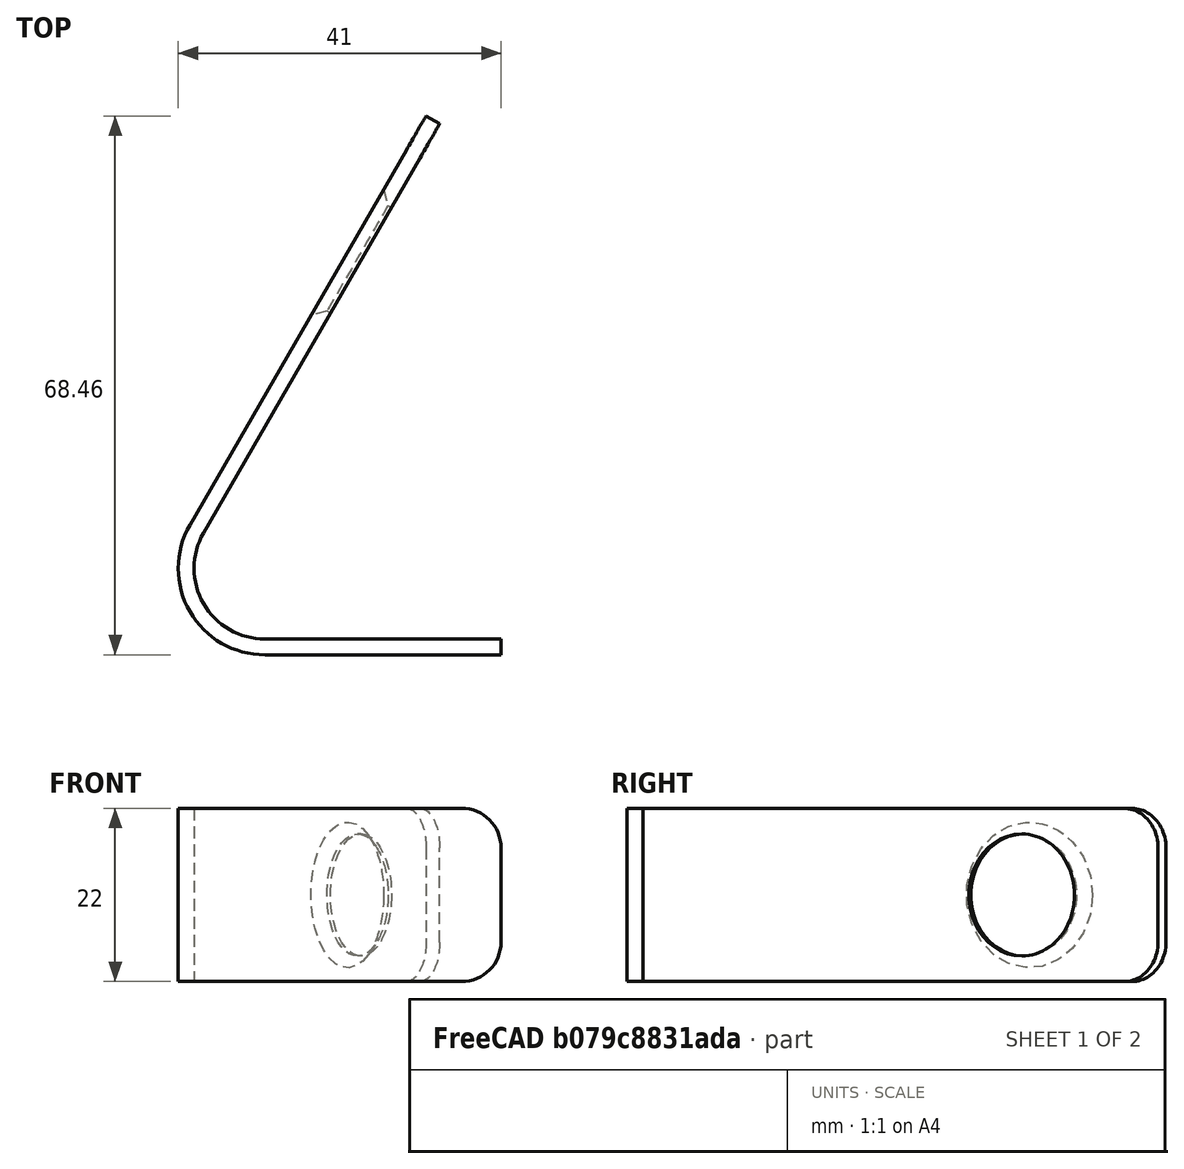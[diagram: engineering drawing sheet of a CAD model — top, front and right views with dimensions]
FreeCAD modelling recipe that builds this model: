
FCSTD DOCUMENT  (FreeCAD 2021.1015R24301 +3962 (Git))
Label: plastic_spring_catapult_2
License: All rights reserved
objects: Sketcher::SketchObject×3, Spreadsheet::Sheet×1, PartDesign::AdditivePipe×1, PartDesign::Pocket×1, PartDesign::Chamfer×1, PartDesign::Fillet×1, PartDesign::Body×1, Mesh::Feature×1
note: 16 computed .brp shape members not serialized (recipe doc carries the construction recipe); baked Part::Feature solids carry a one-line shape summary decoded from their .brp

FEATURE [Spreadsheet::Sheet] Spreadsheet
  PythonMode = false
  cells = A1='width; B1(w)=22; A2='thickness; B2(thk)=2; A3='dia; B3(dia)=10; A4=arm length; B4(l_arm)=60; A5=base length; B5(base_length)=30; A6=catapult angle; B6(a_catapult)=60; A7=bottom curve diameter; B7(dia_bot)=20; A8='marble_diameter; B8(d_marble)=16.4; A9=depth of marble pocket; B9(cup_depth)=8; A10=cup distance from end of arm; B10(l_cup)=20; A11=cup dia; B11(d_cup)=15.5
FEATURE [Sketcher::SketchObject] Sketch  label="profile"
  FullyConstrained = true
  MapMode = 5
  Placement = pos=(0,0,0) rot=(0.57735,0.57735,0.57735;2.0944rad)
  Support = -> [YZ_Plane]
  expr: Constraints[10] = Spreadsheet.thk / 2
  expr: Constraints[11] = Spreadsheet.thk
  expr: Constraints[9] = Spreadsheet.w
  sketch-geometry (4):
    g0: LineSegment StartX=-1 StartY=0 StartZ=0 EndX=1 EndY=0 EndZ=0
    g1: LineSegment StartX=1 StartY=0 StartZ=0 EndX=1 EndY=22 EndZ=0
    g2: LineSegment StartX=1 StartY=22 StartZ=0 EndX=-1 EndY=22 EndZ=0
    g3: LineSegment StartX=-1 StartY=22 StartZ=0 EndX=-1 EndY=0 EndZ=0
  constraints (12):
    c: Coincident(g0,g1)
    c: Coincident(g1,g2)
    c: Coincident(g2,g3)
    c: Coincident(g3,g0)
    c: Horizontal(g0)
    c: Horizontal(g2)
    c: Vertical(g1)
    c: Vertical(g3)
    c: PointOnObject(g0,g-1)
    c: DistanceY(g3,g3) = 22
    c: DistanceX(g0,g-1) = 1
    c: DistanceX(g0,g0) = 2
FEATURE [Sketcher::SketchObject] Sketch001  label="path"
  FullyConstrained = true
  MapMode = 5
  Support = -> [XY_Plane]
  expr: Constraints[3] = Spreadsheet.base_length
  expr: Constraints[5] = Spreadsheet.dia_bot
  expr: Constraints[6] = Spreadsheet.l_arm
  expr: Constraints[7] = Spreadsheet.a_catapult
  sketch-geometry (3):
    g0: LineSegment StartX=0 StartY=0 StartZ=0 EndX=-30 EndY=4.8e-14 EndZ=0
    g1: ArcOfCircle CenterX=-30 CenterY=10 CenterZ=0 NormalX=0 NormalY=0 NormalZ=1 AngleXU=0 Radius=10 StartAngle=2.618 EndAngle=4.71239
    g2: LineSegment StartX=-38.6603 StartY=15 StartZ=0 EndX=-8.66027 EndY=66.9615 EndZ=0
  constraints (10):
    c: Coincident(g0,g-1)
    c: PointOnObject(g0,g-1)
    c: Coincident(g1,g0)
    c: DistanceX(g0,g0) = 30
    c: Tangent(g1,g0)
    c: Diameter(g1) = 20
    c: Distance(g2) = 60
    c: Angle(g0,g2) = 1.0472
    c: Coincident(g1,g2)
    c: Tangent(g1,g2)
FEATURE [PartDesign::AdditivePipe] AdditivePipe
  AuxilleryCurvelinear = true
  AuxillerySpineTangent = false
  Binormal = (0,0,0)
  ClaimChildren = false
  Fit = 0
  FitJoin = 0
  InnerFit = 0
  InnerFitJoin = 0
  Mode = 0
  NewSolid = false
  Placement = pos=(0,0,0) rot=(0.57735,0.57735,0.57735;2.0944rad)
  Profile = -> Sketch
  Spine = -> Sketch001
  SpineTangent = false
  Suppress = false
  Transformation = 0
  Transition = 1
  _ProfileBasedVersion = 1
FEATURE [Sketcher::SketchObject] Sketch002
  ExternalGeometry = -> [AdditivePipe]
  FullyConstrained = true
  MapMode = 5
  Placement = pos=(-36.3564,20.9904,-4.6e-15) rot=(-0.774597,-0.447214,0.447214;1.82348rad)
  Support = -> [AdditivePipe]
  expr: Constraints[0] = Spreadsheet.l_cup
  expr: Constraints[1] = Spreadsheet.w / 2
  expr: Constraints[2] = Spreadsheet.d_cup
  sketch-geometry (1):
    g0: Circle CenterX=33.6602 CenterY=-11 CenterZ=0 NormalX=0 NormalY=0 NormalZ=1 AngleXU=0 Radius=7.75
  constraints (3):
    c: DistanceX(g0,g-3) = 20
    c: DistanceY(g0,g-3) = 11
    c: Diameter(g0) = 15.5
FEATURE [PartDesign::Pocket] Pocket
  BaseFeature = -> AdditivePipe
  ClaimChildren = false
  Fit = 0
  FitJoin = 0
  InnerFit = 0
  InnerFitJoin = 0
  InnerTaperAngle = 0
  InnerTaperAngleRev = 0
  Length = 2
  Length2 = 100
  Linearize = true
  NewSolid = false
  Placement = pos=(0,0,0) rot=(0.57735,0.57735,0.57735;2.0944rad)
  Profile = -> Sketch002
  Suppress = false
  Type = 0
  _ProfileBasedVersion = 1
  expr: Length = Spreadsheet.thk
FEATURE [PartDesign::Chamfer] Chamfer
  Angle = 45
  Base = -> Pocket [Edge30]
  BaseFeature = -> Pocket
  ChamferType = 0
  FlipDirection = false
  NewSolid = false
  Placement = pos=(0,0,0) rot=(0.57735,0.57735,0.57735;2.0944rad)
  Size = 1.5
  Size2 = 1
  SupportTransform = false
  Suppress = false
FEATURE [PartDesign::Fillet] Fillet
  Base = -> Chamfer [Edge10,Edge14,Edge30,Edge31]
  BaseFeature = -> Chamfer
  NewSolid = false
  Placement = pos=(0,0,0) rot=(0.57735,0.57735,0.57735;2.0944rad)
  Radius = 5
  SupportTransform = false
  Suppress = false
FEATURE [PartDesign::Body] Body
  AutoGroupSolids = false
  ExportMode = 0
  Group = -> [Sketch,Sketch001,AdditivePipe,Sketch002,Pocket,Chamfer,Fillet]
  Origin = -> Origin
  Tip = -> Fillet
  _ExportChildren = -> [AdditivePipe,Pocket,Chamfer,Fillet]
  _GroupVersion = 1
FEATURE [Mesh::Feature] Mesh  label="marble_catapult_1"
